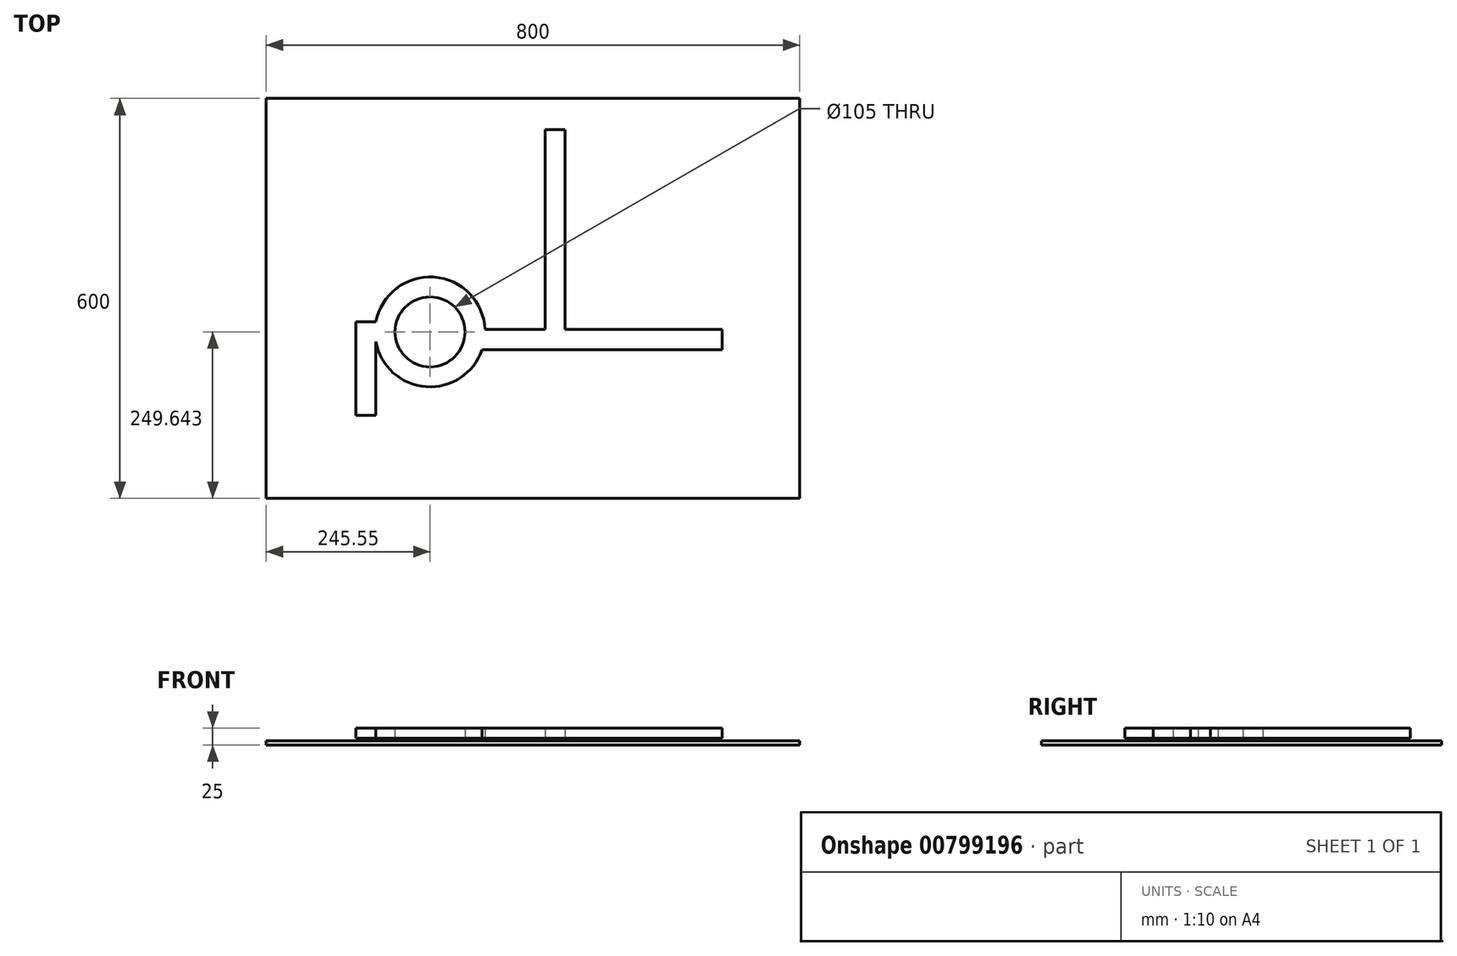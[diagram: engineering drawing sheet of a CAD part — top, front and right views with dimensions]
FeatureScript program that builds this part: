
annotation { "Feature Type Name" : "Feature", "Feature Type Description" : "" }
export const myFeature = defineFeature(function(context is Context, id is Id, definition is map)
    precondition{}
    {
        {
            var Q0;
            Q0=qCreatedBy(makeId("Top.planeOp"),FACE);
            var sketch = newSketch(context, id + "F0", { "sketchPlane" : qUnion([Q0])});
            skLineSegment(sketch, "E0.bottom", {"start": v(403, 314.9) * mm, "end": v(-397, 314.9) * mm});
            skLineSegment(sketch, "E0.top", {"start": v(403, -285.1) * mm, "end": v(-397, -285.1) * mm});
            skLineSegment(sketch, "E0.left", {"start": v(403, 314.9) * mm, "end": v(403, -285.1) * mm});
            skLineSegment(sketch, "E0.right", {"start": v(-397, 314.9) * mm, "end": v(-397, -285.1) * mm});
            skPoint(sketch, "E0.middle", {"position": v(3, 14.9) * mm});
            skSolve(sketch);
        }
        {
            var Q0;
            Q0 = qSketchRegion(id + "F0", true);
            extrude(context, id + "F1", {"entities" : qUnion([Q0]), "depth" : 6 * mm, "offsetDistance" : 25 * mm});
        }
        {
            var Q0;
            Q0=qCreatedBy(makeId("Top.planeOp"),FACE);
            var sketch = newSketch(context, id + "F2", { "sketchPlane" : qUnion([Q0])});
            skLineSegment(sketch, "E1", {"start": v(-262.57, -160.46) * mm, "end": v(-262.57, -20.46) * mm});
            skLineSegment(sketch, "E2", {"start": v(-262.57, -20.46) * mm, "end": v(-232.57, -20.46) * mm});
            skArc(sketch, "E3", {"start": v(-232.57, -50.46) * mm, "mid": v(-157.41, -117.74) * mm, "end": v(-73.33, -62) * mm});
            skCircle(sketch, "E4", {"center": v(-151.45, -35.46) * mm, "radius": 52.5 * mm});
            skLineSegment(sketch, "E5", {"start": v(-69.02, -32) * mm, "end": v(20.98, -32) * mm});
            skLineSegment(sketch, "E6", {"start": v(20.98, -32) * mm, "end": v(20.98, 268) * mm});
            skLineSegment(sketch, "E7", {"start": v(20.98, 268) * mm, "end": v(50.98, 268) * mm});
            skLineSegment(sketch, "E8", {"start": v(50.98, 268) * mm, "end": v(50.98, -32) * mm});
            skLineSegment(sketch, "E9", {"start": v(50.98, -32) * mm, "end": v(286.67, -32) * mm});
            skLineSegment(sketch, "E10", {"start": v(286.67, -32) * mm, "end": v(286.67, -62) * mm});
            skLineSegment(sketch, "E11", {"start": v(286.67, -62) * mm, "end": v(-73.33, -62) * mm});
            skLineSegment(sketch, "E12", {"start": v(-262.57, -160.46) * mm, "end": v(-232.57, -160.46) * mm});
            skLineSegment(sketch, "E13", {"start": v(-232.57, -160.46) * mm, "end": v(-232.57, -50.46) * mm});
            skArc(sketch, "E14.trimOffspring", {"start": v(-69.02, -32) * mm, "mid": v(-145.64, 46.84) * mm, "end": v(-232.57, -20.46) * mm});
            skSolve(sketch);
        }
        {
            var Q0;
            Q0 = qSketchRegion(id + "F2", true);
            extrude(context, id + "F3", {"entities" : qUnion([Q0]), "operationType" : NewBodyOperationType.ADD, "depth" : 25 * mm, "offsetDistance" : 25 * mm, "hasSecondDirection" : true, "secondDirectionOppositeDirection" : true, "secondDirectionDepth" : -10 * mm});
        }
    });
